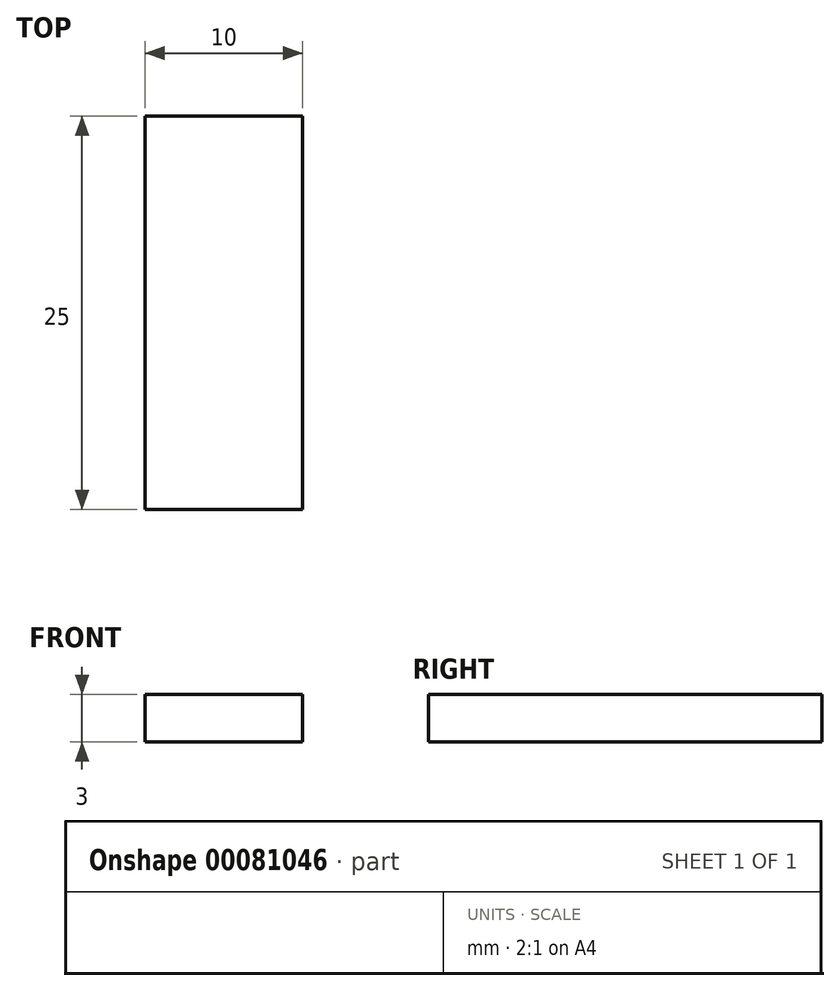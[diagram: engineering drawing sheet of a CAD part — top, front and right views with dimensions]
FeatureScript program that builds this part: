
annotation { "Feature Type Name" : "Feature", "Feature Type Description" : "" }
export const myFeature = defineFeature(function(context is Context, id is Id, definition is map)
    precondition{}
    {
        {
            var Q0;
            Q0=qCreatedBy(makeId("Front.planeOp"),FACE);
            var sketch = newSketch(context, id + "F0", { "sketchPlane" : qUnion([Q0])});
            skLineSegment(sketch, "E0.bottom", {"start": v(-8, 30.44) * mm, "end": v(2, 30.44) * mm});
            skLineSegment(sketch, "E0.top", {"start": v(-8, 27.44) * mm, "end": v(2, 27.44) * mm});
            skLineSegment(sketch, "E0.left", {"start": v(-8, 30.44) * mm, "end": v(-8, 27.44) * mm});
            skLineSegment(sketch, "E0.right", {"start": v(2, 30.44) * mm, "end": v(2, 27.44) * mm});
            skLineSegment(sketch, "E1.bottom", {"start": v(-8, 30.44) * mm, "end": v(0, 30.44) * mm});
            skLineSegment(sketch, "E1.top", {"start": v(-8, 33.44) * mm, "end": v(0, 33.44) * mm});
            skLineSegment(sketch, "E1.left", {"start": v(-8, 30.44) * mm, "end": v(-8, 33.44) * mm});
            skLineSegment(sketch, "E1.right", {"start": v(0, 30.44) * mm, "end": v(0, 33.44) * mm});
            skLineSegment(sketch, "E2.bottom", {"start": v(-8.38, 36.44) * mm, "end": v(-2.38, 36.44) * mm});
            skLineSegment(sketch, "E2.top", {"start": v(-8.38, 33.44) * mm, "end": v(-2.38, 33.44) * mm});
            skLineSegment(sketch, "E2.left", {"start": v(-8.38, 36.44) * mm, "end": v(-8.38, 33.44) * mm});
            skLineSegment(sketch, "E2.right", {"start": v(-2.38, 36.44) * mm, "end": v(-2.38, 33.44) * mm});
            skLineSegment(sketch, "E3.bottom", {"start": v(-8.38, 36.44) * mm, "end": v(-8.38, 36.44) * mm});
            skLineSegment(sketch, "E3.top", {"start": v(-8.38, 34.94) * mm, "end": v(-8.38, 34.94) * mm});
            skLineSegment(sketch, "E3.left", {"start": v(-8.38, 36.44) * mm, "end": v(-8.38, 34.94) * mm});
            skLineSegment(sketch, "E3.right", {"start": v(-8.38, 36.44) * mm, "end": v(-8.38, 34.94) * mm});
            skSolve(sketch);
        }
        {
            var Q0;
            Q0=makeQuery(id+"F0.imprint","IMPRINT",FACE,{"disambiguationData":[TD([[makeQuery(id+"F0.imprint","IMPRINT",EDGE,{"derivedFrom":sQuery(id+"F0.wireOp",EDGE,"E0.bottom")}),-1.0]])]});
            extrude(context, id + "F1", {"entities" : qUnion([Q0]), "endBound" : BoundingType.SYMMETRIC, "depth" : 25 * mm});
        }
    });
